# Revit family: Supply_Fan-BroanNutone-Fresh_In-Premium-FIN-180P
name_source: partatom
category: Mechanical Equipment
units: mm (PartAtom-declared; Revit-internal decimal feet)

## family parameters
Cut with Voids When Loaded = Yes
Host = Face
OmniClass Number = 23.75.35.17.17
OmniClass Title = Room Air Circulation Fans
Part Type = Normal
Room Calculation Point = No
Round Connector Dimension = Use Radius
Shared = No

## types (1)
- Not a Type - Load Type Catalog
    Air Volume = 180 CFM
    Apparent Load = 0 VA
    Assembly Code = E1090900
    Cover Finish = Metal - Broan NuTone - Stainless Steel
    Default Elevation = 0"
    Description = Broan® FRESH IN™ Premium Supply Fan 180 CFM, POWER CORD
    Electrical Connector = Electrical Connection
    Exhaust Diameter = 6"
    Exhaust Radius = 3"
    Fan Wattage = 40 W
    Frequency = 60 Hz
    Length = 14 3/4"
    Manufacturer = Broan
    Model = FIN-180P
    Number of Poles = 1
    Phase = 1
    Power Factor = 1
    Product Documentation Link = https://www.broan-nutone.com
    Product Name = Broan® FRESH IN™ Premium Supply Fan 180 CFM, POWER CORD
    Product Page URL = https://www.broan-nutone.com
    Supply Connector = Supply Connection
    URL = https://www.broan-nutone.com
    Voltage = 120 V
    Width = 10 1/4"

## geometry (parser evidence)
native form markers: Sweep x2
no freeform markers — native parametric forms only
